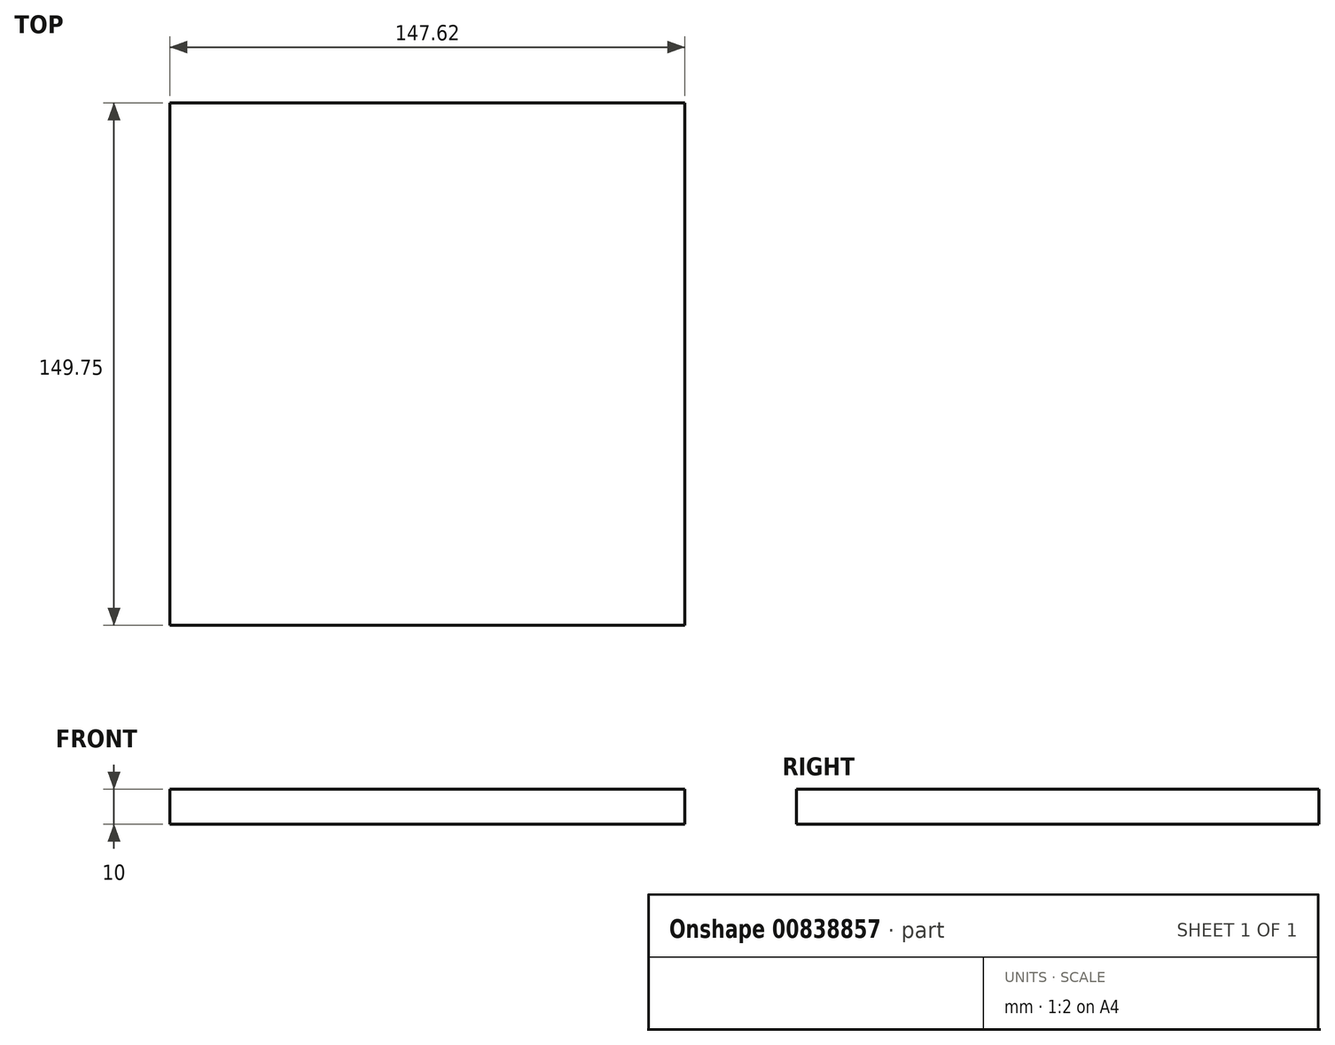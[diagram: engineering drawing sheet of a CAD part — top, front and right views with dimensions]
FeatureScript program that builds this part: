
annotation { "Feature Type Name" : "Feature", "Feature Type Description" : "" }
export const myFeature = defineFeature(function(context is Context, id is Id, definition is map)
    precondition{}
    {
        {
            var Q0;
            Q0=qCreatedBy(makeId("Top.planeOp"),FACE);
            var sketch = newSketch(context, id + "F0", { "sketchPlane" : qUnion([Q0])});
            skLineSegment(sketch, "E0.bottom", {"start": v(-74, -74.23) * mm, "end": v(73.63, -74.23) * mm});
            skLineSegment(sketch, "E0.top", {"start": v(-74, 75.52) * mm, "end": v(73.63, 75.52) * mm});
            skLineSegment(sketch, "E0.left", {"start": v(-74, -74.23) * mm, "end": v(-74, 75.52) * mm});
            skLineSegment(sketch, "E0.right", {"start": v(73.63, -74.23) * mm, "end": v(73.63, 75.52) * mm});
            skSolve(sketch);
        }
        {
            var Q0;
            Q0=makeQuery(id+"F0.imprint","IMPRINT",FACE,{"disambiguationData":[TD([[makeQuery(id+"F0.imprint","IMPRINT",EDGE,{"derivedFrom":sQuery(id+"F0.wireOp",EDGE,"E0.bottom")}),1.0]])]});
            extrude(context, id + "F1", {"entities" : qUnion([Q0]), "depth" : 10 * mm, "offsetDistance" : 25 * mm});
        }
    });
